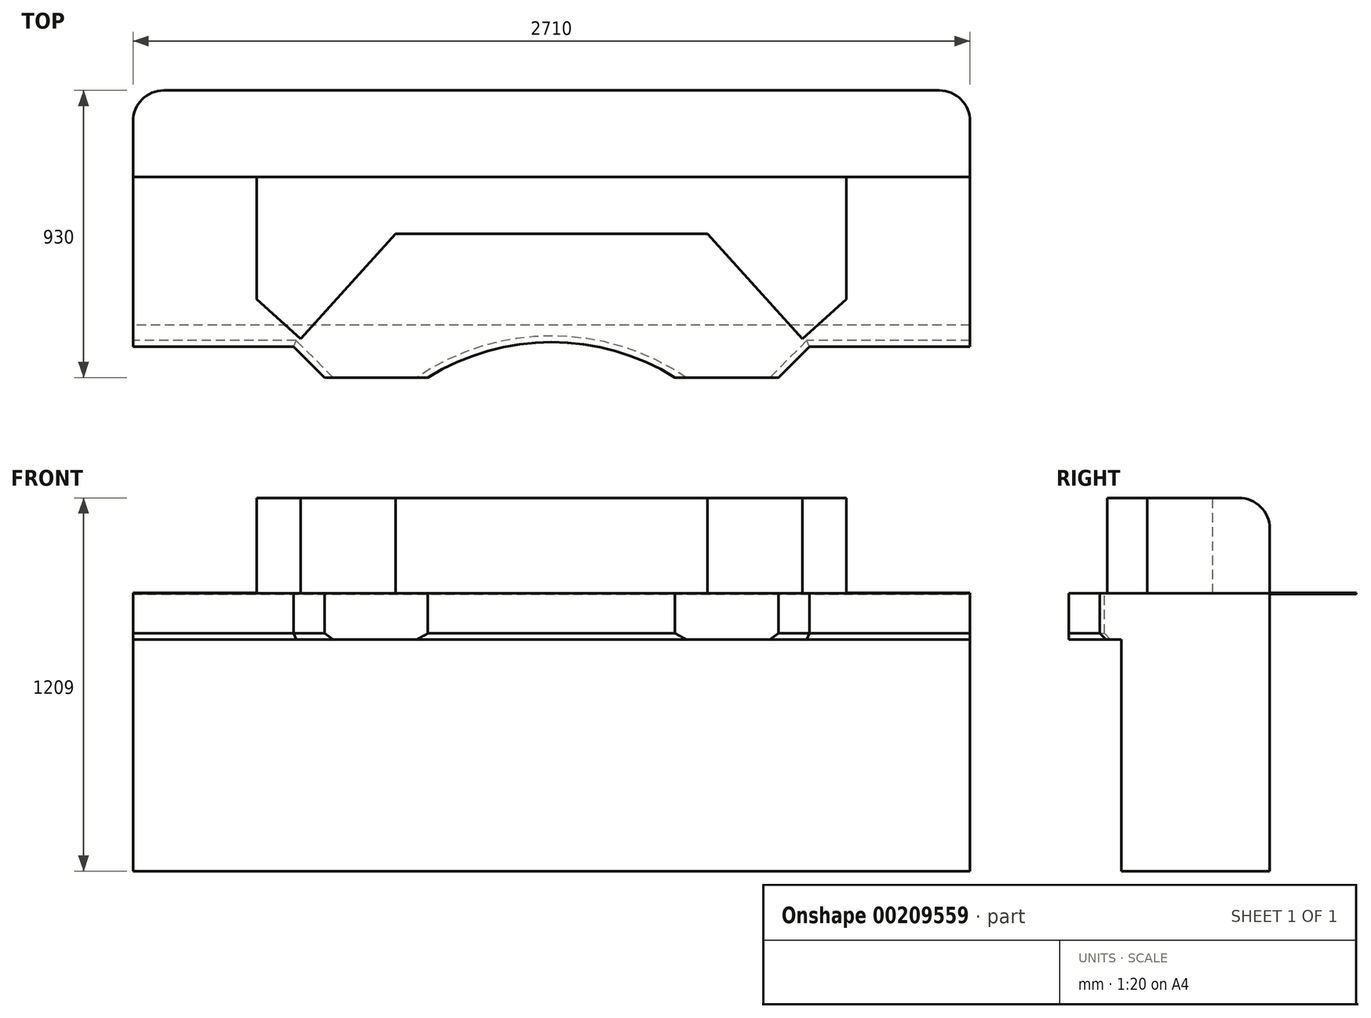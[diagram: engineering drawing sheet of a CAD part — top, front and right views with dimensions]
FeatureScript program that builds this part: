
annotation { "Feature Type Name" : "Feature", "Feature Type Description" : "" }
export const myFeature = defineFeature(function(context is Context, id is Id, definition is map)
    precondition{}
    {
        {
            var Q0;
            Q0=qCreatedBy(makeId("Top.planeOp"),FACE);
            var sketch = newSketch(context, id + "F0", { "sketchPlane" : qUnion([Q0])});
            skLineSegment(sketch, "E0.bottom", {"start": v(1355, -325) * mm, "end": v(-1355, -325) * mm});
            skLineSegment(sketch, "E0.top", {"start": v(1355, 325) * mm, "end": v(-1355, 325) * mm});
            skLineSegment(sketch, "E0.left", {"start": v(1355, -325) * mm, "end": v(1355, 325) * mm});
            skLineSegment(sketch, "E0.right", {"start": v(-1355, -325) * mm, "end": v(-1355, 325) * mm});
            skPoint(sketch, "E0.middle", {"position": v(0, 0) * mm});
            skSolve(sketch);
        }
        {
            var Q0;
            Q0 = qSketchRegion(id + "F0", true);
            extrude(context, id + "F1", {"entities" : qUnion([Q0]), "depth" : 1209 * mm});
        }
        {
            var Q0;
            Q0=makeQuery(id+"F1.opExtrude","SWEPT_FACE",FACE,{"disambiguationData":[OSD([sQuery(id+"F0.wireOp",EDGE,"E0.bottom")])]});
            var sketch = newSketch(context, id + "F2", { "sketchPlane" : qUnion([Q0])});
            skLineSegment(sketch, "E1", {"start": v(0, 1209) * mm, "end": v(0, 0) * mm, "construction": true});
            skLineSegment(sketch, "E2.bottom", {"start": v(-1355, 1209) * mm, "end": v(-955, 1209) * mm});
            skLineSegment(sketch, "E2.top", {"start": v(-1355, 900) * mm, "end": v(-955, 900) * mm});
            skLineSegment(sketch, "E2.left", {"start": v(-1355, 1209) * mm, "end": v(-1355, 900) * mm});
            skLineSegment(sketch, "E2.right", {"start": v(-955, 1209) * mm, "end": v(-955, 900) * mm});
            skLineSegment(sketch, "E3.MirrorCS", {"start": v(1355, 900) * mm, "end": v(955, 900) * mm});
            skLineSegment(sketch, "E4.MirrorCS", {"start": v(1355, 1209) * mm, "end": v(955, 1209) * mm});
            skLineSegment(sketch, "E5.MirrorCS", {"start": v(955, 1209) * mm, "end": v(955, 900) * mm});
            skLineSegment(sketch, "E6.MirrorCS", {"start": v(1355, 1209) * mm, "end": v(1355, 900) * mm});
            skSolve(sketch);
        }
        {
            var Q0;
            Q0 = qSketchRegion(id + "F2", true);
            extrude(context, id + "F3", {"entities" : qUnion([Q0]), "operationType" : NewBodyOperationType.REMOVE, "endBound" : BoundingType.THROUGH_ALL, "oppositeDirection" : true, "depth" : 25 * mm});
        }
        {
            var Q0;
            Q0=makeQuery(id+"F3.boolean.opBoolean","COPY",FACE,{"derivedFrom":makeQuery(id+"F3.opExtrude","SWEPT_FACE",FACE,{"disambiguationData":[OSD([sQuery(id+"F2.wireOp",EDGE,"E2.top")])]})});
            var sketch = newSketch(context, id + "F4", { "sketchPlane" : qUnion([Q0])});
            skPoint(sketch, "E7.0", {"position": v(1355, 325) * mm});
            skLineSegment(sketch, "E8", {"start": v(-1355, 325) * mm, "end": v(1355, 325) * mm});
            skLineSegment(sketch, "E9", {"start": v(-1355, 325) * mm, "end": v(-1355, 505) * mm});
            skArc(sketch, "E10", {"start": v(-1255, 605) * mm, "mid": v(-1325.71, 575.71) * mm, "end": v(-1355, 505) * mm});
            skLineSegment(sketch, "E11", {"start": v(-1355, 505) * mm, "end": v(-1255, 505) * mm, "construction": true});
            skLineSegment(sketch, "E12", {"start": v(-1255, 505) * mm, "end": v(-1255, 605) * mm, "construction": true});
            skLineSegment(sketch, "E13", {"start": v(0, 325) * mm, "end": v(0, 0) * mm, "construction": true});
            skLineSegment(sketch, "E14", {"start": v(-1255, 605) * mm, "end": v(0, 605) * mm});
            skLineSegment(sketch, "E15.MirrorCS", {"start": v(1255, 605) * mm, "end": v(0, 605) * mm});
            skArc(sketch, "E16.MirrorCS", {"start": v(1255, 605) * mm, "mid": v(1325.71, 575.71) * mm, "end": v(1355, 505) * mm});
            skLineSegment(sketch, "E17.MirrorCS", {"start": v(1355, 325) * mm, "end": v(1355, 505) * mm});
            skSolve(sketch);
        }
        {
            var Q0;
            Q0 = qSketchRegion(id + "F4", true);
            extrude(context, id + "F5", {"entities" : qUnion([Q0]), "operationType" : NewBodyOperationType.ADD, "oppositeDirection" : true, "depth" : 3 * mm, "hasSecondDirection" : true, "secondDirectionOppositeDirection" : false, "secondDirectionDepth" : 1 * mm});
        }
        {
            var Q0;
            Q0=makeQuery(id+"F5.boolean.opBoolean","MERGE",FACE,{"derivedFrom":[makeQuery(id+"F1.opExtrude","SWEPT_FACE",FACE,{"disambiguationData":[OSD([sQuery(id+"F0.wireOp",EDGE,"E0.right")])]}),makeQuery(id+"F5.opExtrude","SWEPT_FACE",FACE,{"disambiguationData":[OSD([sQuery(id+"F4.wireOp",EDGE,"E9")])]})]});
            var sketch = newSketch(context, id + "F6", { "sketchPlane" : qUnion([Q0])});
            skLineSegment(sketch, "E18.bottom", {"start": v(325, 0) * mm, "end": v(155, 0) * mm});
            skLineSegment(sketch, "E18.top", {"start": v(325, 750) * mm, "end": v(155, 750) * mm});
            skLineSegment(sketch, "E18.left", {"start": v(325, 0) * mm, "end": v(325, 750) * mm});
            skLineSegment(sketch, "E18.right", {"start": v(155, 0) * mm, "end": v(155, 750) * mm});
            skSolve(sketch);
        }
        {
            var Q0;
            Q0 = qSketchRegion(id + "F6", true);
            extrude(context, id + "F7", {"entities" : qUnion([Q0]), "operationType" : NewBodyOperationType.REMOVE, "endBound" : BoundingType.THROUGH_ALL, "oppositeDirection" : true, "depth" : 25 * mm});
        }
        {
            var Q0;
            Q0=makeQuery(id+"F1.opExtrude","CAP_EDGE",EDGE,{"disambiguationData":[OSD([sQuery(id+"F0.wireOp",EDGE,"E0.top")])],"isStart":false});
            fillet(context, id + "F8", {"entities" : qUnion([Q0]), "radius" : 100 * mm, "tangentPropagation" : true, "allowEdgeOverflow" : false});
        }
        {
            var Q0;
            Q0=makeQuery(id+"F1.opExtrude","CAP_FACE",FACE,{"disambiguationData":[OSD([sQuery(id+"F0.wireOp",EDGE,"E0.bottom"),sQuery(id+"F0.wireOp",EDGE,"E0.top"),sQuery(id+"F0.wireOp",EDGE,"E0.left"),sQuery(id+"F0.wireOp",EDGE,"E0.right")])],"isStart":false});
            var sketch = newSketch(context, id + "F9", { "sketchPlane" : qUnion([Q0])});
            skLineSegment(sketch, "E19", {"start": v(-955, -71.87) * mm, "end": v(-811.75, -200.42) * mm});
            skLineSegment(sketch, "E20", {"start": v(-811.75, -200.42) * mm, "end": v(-504.42, 140.2) * mm});
            skLineSegment(sketch, "E21", {"start": v(-504.42, 140.2) * mm, "end": v(0, 140.2) * mm});
            skLineSegment(sketch, "E22", {"start": v(0, 225) * mm, "end": v(0, 0) * mm, "construction": true});
            skLineSegment(sketch, "E23.MirrorCS", {"start": v(504.42, 140.2) * mm, "end": v(0, 140.2) * mm});
            skLineSegment(sketch, "E24.MirrorCS", {"start": v(955, -71.87) * mm, "end": v(811.75, -200.42) * mm});
            skLineSegment(sketch, "E25.MirrorCS", {"start": v(811.75, -200.42) * mm, "end": v(504.42, 140.2) * mm});
            skLineSegment(sketch, "E26", {"start": v(-955, -71.87) * mm, "end": v(-955, -325) * mm});
            skLineSegment(sketch, "E27", {"start": v(-955, -325) * mm, "end": v(0, -325) * mm});
            skLineSegment(sketch, "E28.MirrorCS", {"start": v(955, -325) * mm, "end": v(0, -325) * mm});
            skLineSegment(sketch, "E29.MirrorCS", {"start": v(955, -71.87) * mm, "end": v(955, -325) * mm});
            skSolve(sketch);
        }
        {
            var Q0;
            Q0 = qSketchRegion(id + "F9", true);
            var Q1;
            Q1=makeQuery(id+"F3.boolean.opBoolean","COPY",FACE,{"derivedFrom":makeQuery(id+"F3.opExtrude","SWEPT_FACE",FACE,{"disambiguationData":[OSD([sQuery(id+"F2.wireOp",EDGE,"E2.top")])]})});
            extrude(context, id + "F10", {"entities" : qUnion([Q0]), "operationType" : NewBodyOperationType.REMOVE, "endBound" : BoundingType.UP_TO_SURFACE, "oppositeDirection" : true, "endBoundEntityFace" : qUnion([Q1]), "depth" : 25 * mm});
        }
        {
            var Q0;
            {var subQ0=sQuery(id+"F2.wireOp",EDGE,"E2.top");Q0=makeQuery(id+"F10.boolean.opBoolean","MERGE",FACE,{"derivedFrom":[makeQuery(id+"F3.boolean.opBoolean","COPY",FACE,{"derivedFrom":makeQuery(id+"F3.opExtrude","SWEPT_FACE",FACE,{"disambiguationData":[OSD([subQ0])]})}),makeQuery(id+"F3.boolean.opBoolean","COPY",FACE,{"derivedFrom":makeQuery(id+"F3.opExtrude","SWEPT_FACE",FACE,{"disambiguationData":[OSD([sQuery(id+"F2.wireOp",EDGE,"E3.MirrorCS")])]})}),makeQuery(id+"F10.opExtrude","CAP_FACE",FACE,{"disambiguationData":[OSD([subQ0])],"isStart":false})]});}
            var sketch = newSketch(context, id + "F11", { "sketchPlane" : qUnion([Q0])});
            skLineSegment(sketch, "E30", {"start": v(0, 0) * mm, "end": v(0, -325) * mm, "construction": true});
            skArc(sketch, "E31", {"start": v(400, -325) * mm, "mid": v(0, -210.44) * mm, "end": v(-400, -325) * mm});
            skLineSegment(sketch, "E32", {"start": v(0, -325) * mm, "end": v(0, -966.04) * mm, "construction": true});
            skLineSegment(sketch, "E33", {"start": v(-835, -225) * mm, "end": v(-1355, -225) * mm});
            skLineSegment(sketch, "E34", {"start": v(-1355, -225) * mm, "end": v(-1355, -325) * mm});
            skLineSegment(sketch, "E35", {"start": v(-1355, -325) * mm, "end": v(-735, -325) * mm});
            skLineSegment(sketch, "E36", {"start": v(-400, -325) * mm, "end": v(400, -325) * mm});
            skLineSegment(sketch, "E37", {"start": v(-835, -225) * mm, "end": v(-735, -325) * mm});
            skLineSegment(sketch, "E38.MirrorCS", {"start": v(835, -225) * mm, "end": v(1355, -225) * mm});
            skLineSegment(sketch, "E39.MirrorCS", {"start": v(1355, -325) * mm, "end": v(735, -325) * mm});
            skLineSegment(sketch, "E40.MirrorCS", {"start": v(835, -225) * mm, "end": v(735, -325) * mm});
            skLineSegment(sketch, "E41.MirrorCS", {"start": v(1355, -225) * mm, "end": v(1355, -325) * mm});
            skSolve(sketch);
        }
        {
            var Q0;
            Q0 = qSketchRegion(id + "F11", true);
            extrude(context, id + "F12", {"entities" : qUnion([Q0]), "operationType" : NewBodyOperationType.REMOVE, "endBound" : BoundingType.THROUGH_ALL, "oppositeDirection" : true, "depth" : 25 * mm});
        }
        {
            var Q0;
            Q0=makeQuery(id+"F12.boolean.opBoolean","COPY",EDGE,{"derivedFrom":makeQuery(id+"F12.opExtrude","CAP_EDGE",EDGE,{"disambiguationData":[OSD([sQuery(id+"F11.wireOp",EDGE,"E33")])],"isStart":true})});
            var Q1;
            Q1=makeQuery(id+"F12.boolean.opBoolean","COPY",EDGE,{"derivedFrom":makeQuery(id+"F12.opExtrude","CAP_EDGE",EDGE,{"disambiguationData":[OSD([sQuery(id+"F11.wireOp",EDGE,"E37")])],"isStart":true})});
            var Q2;
            {var subQ0=sQuery(id+"F2.wireOp",EDGE,"E2.top");var subQ1=sQuery(id+"F2.wireOp",EDGE,"E3.MirrorCS");var subQ2=makeQuery(id+"F3.boolean.opBoolean","COPY",FACE,{"derivedFrom":makeQuery(id+"F3.opExtrude","SWEPT_FACE",FACE,{"disambiguationData":[OSD([subQ0])]})});Q2=makeQuery(id+"F12.boolean.opBoolean","SPLIT",EDGE,{"disambiguationData":[TD([makeQuery(id+"F12.opExtrude","SWEPT_FACE",FACE,{"disambiguationData":[OSD([sQuery(id+"F11.wireOp",EDGE,"E37")])]})])],"derivedFrom":makeQuery(id+"F10.boolean.opBoolean","MERGE",EDGE,{"derivedFrom":[makeQuery(id+"F3.boolean.opBoolean","COPY",EDGE,{"derivedFrom":makeQuery(id+"F3.opExtrude","CAP_EDGE",EDGE,{"disambiguationData":[OSD([subQ0])],"isStart":true})}),makeQuery(id+"F3.boolean.opBoolean","COPY",EDGE,{"derivedFrom":makeQuery(id+"F3.opExtrude","CAP_EDGE",EDGE,{"disambiguationData":[OSD([subQ1])],"isStart":true})}),makeQuery(id+"F10.opExtrude","TWEAK_EDGE",EDGE,{"derivedFrom":[subQ2,makeQuery(id+"F9.imprint","IMPRINT",EDGE,{"derivedFrom":sQuery(id+"F9.wireOp",EDGE,"E27")}),makeQuery(id+"F9.imprint","IMPRINT",EDGE,{"derivedFrom":sQuery(id+"F9.wireOp",EDGE,"E28.MirrorCS")})]})]})});}
            var Q3;
            Q3=makeQuery(id+"F12.boolean.opBoolean","COPY",EDGE,{"derivedFrom":makeQuery(id+"F12.opExtrude","CAP_EDGE",EDGE,{"disambiguationData":[OSD([sQuery(id+"F11.wireOp",EDGE,"E31")])],"isStart":true})});
            var Q4;
            {var subQ0=sQuery(id+"F2.wireOp",EDGE,"E2.top");var subQ1=sQuery(id+"F2.wireOp",EDGE,"E3.MirrorCS");var subQ2=makeQuery(id+"F3.boolean.opBoolean","COPY",FACE,{"derivedFrom":makeQuery(id+"F3.opExtrude","SWEPT_FACE",FACE,{"disambiguationData":[OSD([subQ0])]})});Q4=makeQuery(id+"F12.boolean.opBoolean","SPLIT",EDGE,{"disambiguationData":[TD([makeQuery(id+"F12.opExtrude","SWEPT_FACE",FACE,{"disambiguationData":[OSD([sQuery(id+"F11.wireOp",EDGE,"E40.MirrorCS")])]})])],"derivedFrom":makeQuery(id+"F10.boolean.opBoolean","MERGE",EDGE,{"derivedFrom":[makeQuery(id+"F3.boolean.opBoolean","COPY",EDGE,{"derivedFrom":makeQuery(id+"F3.opExtrude","CAP_EDGE",EDGE,{"disambiguationData":[OSD([subQ0])],"isStart":true})}),makeQuery(id+"F3.boolean.opBoolean","COPY",EDGE,{"derivedFrom":makeQuery(id+"F3.opExtrude","CAP_EDGE",EDGE,{"disambiguationData":[OSD([subQ1])],"isStart":true})}),makeQuery(id+"F10.opExtrude","TWEAK_EDGE",EDGE,{"derivedFrom":[subQ2,makeQuery(id+"F9.imprint","IMPRINT",EDGE,{"derivedFrom":sQuery(id+"F9.wireOp",EDGE,"E27")}),makeQuery(id+"F9.imprint","IMPRINT",EDGE,{"derivedFrom":sQuery(id+"F9.wireOp",EDGE,"E28.MirrorCS")})]})]})});}
            var Q5;
            Q5=makeQuery(id+"F12.boolean.opBoolean","COPY",EDGE,{"derivedFrom":makeQuery(id+"F12.opExtrude","CAP_EDGE",EDGE,{"disambiguationData":[OSD([sQuery(id+"F11.wireOp",EDGE,"E38.MirrorCS")])],"isStart":true})});
            var Q6;
            Q6=makeQuery(id+"F12.boolean.opBoolean","INTERSECT",EDGE,{"derivedFrom":[makeQuery(id+"F7.boolean.opBoolean","COPY",FACE,{"derivedFrom":makeQuery(id+"F7.opExtrude","SWEPT_FACE",FACE,{"disambiguationData":[OSD([sQuery(id+"F6.wireOp",EDGE,"E18.top")])]})}),makeQuery(id+"F12.opExtrude","SWEPT_FACE",FACE,{"disambiguationData":[OSD([sQuery(id+"F11.wireOp",EDGE,"E33")])]})]});
            var Q7;
            Q7=makeQuery(id+"F12.boolean.opBoolean","INTERSECT",EDGE,{"derivedFrom":[makeQuery(id+"F7.boolean.opBoolean","COPY",FACE,{"derivedFrom":makeQuery(id+"F7.opExtrude","SWEPT_FACE",FACE,{"disambiguationData":[OSD([sQuery(id+"F6.wireOp",EDGE,"E18.top")])]})}),makeQuery(id+"F12.opExtrude","SWEPT_FACE",FACE,{"disambiguationData":[OSD([sQuery(id+"F11.wireOp",EDGE,"E37")])]})]});
            var Q8;
            {var subQ0=sQuery(id+"F0.wireOp",EDGE,"E0.bottom");var subQ1=sQuery(id+"F6.wireOp",EDGE,"E18.top");Q8=makeQuery(id+"F12.boolean.opBoolean","SPLIT",EDGE,{"disambiguationData":[TD([makeQuery(id+"F12.opExtrude","SWEPT_FACE",FACE,{"disambiguationData":[OSD([sQuery(id+"F11.wireOp",EDGE,"E37")])]})])],"derivedFrom":makeQuery(id+"F7.boolean.opBoolean","COPY",EDGE,{"derivedFrom":makeQuery(id+"F7.opExtrude","SWEPT_EDGE",EDGE,{"disambiguationData":[OSD([subQ0,sQuery(id+"F0.wireOp",EDGE,"E0.right"),subQ1,sQuery(id+"F6.wireOp",EDGE,"E18.left")])]})})});}
            var Q9;
            Q9=makeQuery(id+"F12.boolean.opBoolean","INTERSECT",EDGE,{"derivedFrom":[makeQuery(id+"F7.boolean.opBoolean","COPY",FACE,{"derivedFrom":makeQuery(id+"F7.opExtrude","SWEPT_FACE",FACE,{"disambiguationData":[OSD([sQuery(id+"F6.wireOp",EDGE,"E18.top")])]})}),makeQuery(id+"F12.opExtrude","SWEPT_FACE",FACE,{"disambiguationData":[OSD([sQuery(id+"F11.wireOp",EDGE,"E31")])]})]});
            var Q10;
            {var subQ0=sQuery(id+"F0.wireOp",EDGE,"E0.bottom");var subQ1=sQuery(id+"F6.wireOp",EDGE,"E18.top");Q10=makeQuery(id+"F12.boolean.opBoolean","SPLIT",EDGE,{"disambiguationData":[TD([makeQuery(id+"F12.opExtrude","SWEPT_FACE",FACE,{"disambiguationData":[OSD([sQuery(id+"F11.wireOp",EDGE,"E40.MirrorCS")])]})])],"derivedFrom":makeQuery(id+"F7.boolean.opBoolean","COPY",EDGE,{"derivedFrom":makeQuery(id+"F7.opExtrude","SWEPT_EDGE",EDGE,{"disambiguationData":[OSD([subQ0,sQuery(id+"F0.wireOp",EDGE,"E0.right"),subQ1,sQuery(id+"F6.wireOp",EDGE,"E18.left")])]})})});}
            var Q11;
            Q11=makeQuery(id+"F12.boolean.opBoolean","INTERSECT",EDGE,{"derivedFrom":[makeQuery(id+"F7.boolean.opBoolean","COPY",FACE,{"derivedFrom":makeQuery(id+"F7.opExtrude","SWEPT_FACE",FACE,{"disambiguationData":[OSD([sQuery(id+"F6.wireOp",EDGE,"E18.top")])]})}),makeQuery(id+"F12.opExtrude","SWEPT_FACE",FACE,{"disambiguationData":[OSD([sQuery(id+"F11.wireOp",EDGE,"E38.MirrorCS")])]})]});
            var Q12;
            Q12=makeQuery(id+"F12.boolean.opBoolean","COPY",EDGE,{"derivedFrom":makeQuery(id+"F12.opExtrude","CAP_EDGE",EDGE,{"disambiguationData":[OSD([sQuery(id+"F11.wireOp",EDGE,"E40.MirrorCS")])],"isStart":true})});
            var Q13;
            Q13=makeQuery(id+"F12.boolean.opBoolean","INTERSECT",EDGE,{"derivedFrom":[makeQuery(id+"F7.boolean.opBoolean","COPY",FACE,{"derivedFrom":makeQuery(id+"F7.opExtrude","SWEPT_FACE",FACE,{"disambiguationData":[OSD([sQuery(id+"F6.wireOp",EDGE,"E18.top")])]})}),makeQuery(id+"F12.opExtrude","SWEPT_FACE",FACE,{"disambiguationData":[OSD([sQuery(id+"F11.wireOp",EDGE,"E40.MirrorCS")])]})]});
            chamfer(context, id + "F13", {"entities" : qUnion([Q0, Q1, Q2, Q3, Q4, Q5, Q6, Q7, Q8, Q9, Q10, Q11, Q12, Q13]), "width" : 20 * mm, "tangentPropagation" : true});
        }
    });
